FCSTD DOCUMENT  (FreeCAD 1.0R39109 (Git))
Label: bass
License: All rights reserved
LicenseURL: https://en.wikipedia.org/wiki/All_rights_reserved
objects: Sketcher::SketchObject×1, PartDesign::Body×1
note: 3 computed .brp shape members not serialized (recipe doc carries the construction recipe); baked Part::Feature solids carry a one-line shape summary decoded from their .brp

FEATURE [Sketcher::SketchObject] Sketch
  ArcFitTolerance = 1e-06
  AttachmentSupport = -> [XY_Plane]
  FullyConstrained = true
  MakeInternals = false
  MapMode = 5
  sketch-geometry (43):
    g0: LineSegment StartX=-100 StartY=100 StartZ=0 EndX=-100 EndY=21.5 EndZ=0
    g1: LineSegment StartX=-100 StartY=-100 StartZ=0 EndX=20 EndY=-100 EndZ=0
    g2: LineSegment StartX=100 StartY=-20 StartZ=0 EndX=100 EndY=100 EndZ=0
    g3: LineSegment StartX=100 StartY=100 StartZ=0 EndX=-100 EndY=100 EndZ=0
    g4: Circle CenterX=-82.5 CenterY=-82.5 CenterZ=0 NormalX=0 NormalY=0 NormalZ=1 AngleXU=0 Radius=4
    g5: LineSegment [constr] StartX=-95 StartY=-70 StartZ=0 EndX=-95 EndY=-95 EndZ=0
    g6: LineSegment [constr] StartX=-95 StartY=-95 StartZ=0 EndX=-70 EndY=-95 EndZ=0
    g7: LineSegment [constr] StartX=-70 StartY=-95 StartZ=0 EndX=-70 EndY=-70 EndZ=0
    g8: LineSegment [constr] StartX=-70 StartY=-70 StartZ=0 EndX=-95 EndY=-70 EndZ=0
    g9: Circle [constr] CenterX=-95 CenterY=-95 CenterZ=0 NormalX=0 NormalY=0 NormalZ=1 AngleXU=0 Radius=1.5
    g10: Circle [constr] CenterX=-95 CenterY=-70 CenterZ=0 NormalX=0 NormalY=0 NormalZ=1 AngleXU=0 Radius=1.5
    g11: Circle [constr] CenterX=-70 CenterY=-70 CenterZ=0 NormalX=0 NormalY=0 NormalZ=1 AngleXU=0 Radius=1.5
    g12: Circle [constr] CenterX=-70 CenterY=-95 CenterZ=0 NormalX=0 NormalY=0 NormalZ=1 AngleXU=0 Radius=1.5
    g13: LineSegment [constr] StartX=-95 StartY=95 StartZ=0 EndX=-95 EndY=70 EndZ=0
    g14: LineSegment [constr] StartX=-95 StartY=70 StartZ=0 EndX=-70 EndY=70 EndZ=0
    g15: LineSegment [constr] StartX=-70 StartY=70 StartZ=0 EndX=-70 EndY=95 EndZ=0
    g16: LineSegment [constr] StartX=-70 StartY=95 StartZ=0 EndX=-95 EndY=95 EndZ=0
    g17: Circle [constr] CenterX=-95 CenterY=95 CenterZ=0 NormalX=0 NormalY=0 NormalZ=1 AngleXU=0 Radius=1.5
    g18: Circle [constr] CenterX=-70 CenterY=95 CenterZ=0 NormalX=0 NormalY=0 NormalZ=1 AngleXU=0 Radius=1.5
    g19: Circle [constr] CenterX=-70 CenterY=70 CenterZ=0 NormalX=0 NormalY=0 NormalZ=1 AngleXU=0 Radius=1.5
    g20: Circle [constr] CenterX=-95 CenterY=70 CenterZ=0 NormalX=0 NormalY=0 NormalZ=1 AngleXU=0 Radius=1.5
    g21: Circle CenterX=-82.5 CenterY=82.5 CenterZ=0 NormalX=0 NormalY=0 NormalZ=1 AngleXU=0 Radius=4
    g22: LineSegment [constr] StartX=70 StartY=95 StartZ=0 EndX=70 EndY=70 EndZ=0
    g23: LineSegment [constr] StartX=70 StartY=70 StartZ=0 EndX=95 EndY=70 EndZ=0
    g24: LineSegment [constr] StartX=95 StartY=70 StartZ=0 EndX=95 EndY=95 EndZ=0
    g25: LineSegment [constr] StartX=95 StartY=95 StartZ=0 EndX=70 EndY=95 EndZ=0
    g26: Circle CenterX=82.5 CenterY=82.5 CenterZ=0 NormalX=0 NormalY=0 NormalZ=1 AngleXU=0 Radius=4
    g27: Circle [constr] CenterX=70 CenterY=95 CenterZ=0 NormalX=0 NormalY=0 NormalZ=1 AngleXU=0 Radius=1.5
    g28: Circle [constr] CenterX=95 CenterY=95 CenterZ=0 NormalX=0 NormalY=0 NormalZ=1 AngleXU=0 Radius=1.5
    g29: Circle [constr] CenterX=95 CenterY=70 CenterZ=0 NormalX=0 NormalY=0 NormalZ=1 AngleXU=0 Radius=1.5
    g30: Circle [constr] CenterX=70 CenterY=70 CenterZ=0 NormalX=0 NormalY=0 NormalZ=1 AngleXU=0 Radius=1.5
    g31: LineSegment StartX=-100 StartY=-21.5 StartZ=0 EndX=-64 EndY=-21.5 EndZ=0
    g32: LineSegment StartX=-64 StartY=21.5 StartZ=0 EndX=-100 EndY=21.5 EndZ=0
    g33: LineSegment StartX=-100 StartY=-21.5 StartZ=0 EndX=-100 EndY=-100 EndZ=0
    g34: Circle CenterX=-93 CenterY=-31.5 CenterZ=0 NormalX=0 NormalY=0 NormalZ=1 AngleXU=0 Radius=3.5
    g35: Circle CenterX=-71 CenterY=-31.5 CenterZ=0 NormalX=0 NormalY=0 NormalZ=1 AngleXU=0 Radius=3.5
    g36: Circle CenterX=-93 CenterY=31.5 CenterZ=0 NormalX=0 NormalY=0 NormalZ=1 AngleXU=0 Radius=3.5
    g37: Circle CenterX=-71 CenterY=31.5 CenterZ=0 NormalX=0 NormalY=0 NormalZ=1 AngleXU=0 Radius=3.5
    g38: LineSegment StartX=20 StartY=-100 StartZ=0 EndX=100 EndY=-20 EndZ=0
    g39: LineSegment [constr] StartX=-82 StartY=36.5 StartZ=0 EndX=-82 EndY=-36.5 EndZ=0
    g40: Circle [constr] CenterX=-85.5 CenterY=0 CenterZ=0 NormalX=0 NormalY=0 NormalZ=1 AngleXU=0 Radius=7.5
    g41: LineSegment StartX=-64 StartY=-21.5 StartZ=0 EndX=-64 EndY=21.5 EndZ=0
    g42: Circle CenterX=0 CenterY=0 CenterZ=0 NormalX=0 NormalY=0 NormalZ=1 AngleXU=0 Radius=57.5
  constraints (115):
    c: Coincident(g33,g1)
    c: Coincident(g2,g3)
    c: Coincident(g3,g0)
    c: Vertical(g0)
    c: Vertical(g2)
    c: Horizontal(g1)
    c: Horizontal(g3)
    c: Diameter(g4) = 8
    c: Coincident(g5,g6)
    c: Coincident(g6,g7)
    c: Coincident(g7,g8)
    c: Coincident(g8,g5)
    c: Vertical(g5)
    c: Vertical(g7)
    c: Horizontal(g6)
    c: Horizontal(g8)
    c: Equal(g7,g6)
    c: Symmetric(g5,g6,g4)
    c: Coincident(g9,g5)
    c: Coincident(g10,g5)
    c: Coincident(g11,g7)
    c: Coincident(g12,g6)
    c: Equal(g9,g10)
    c: Equal(g10,g11)
    c: Equal(g11,g12)
    c: Diameter(g12) = 3
    c: DistanceY(g33,g5) = 5
    c: Distance(g5,g0) = 5
    c: DistanceX(g8,g8) = 25
    c: Coincident(g13,g14)
    c: Coincident(g14,g15)
    c: Coincident(g15,g16)
    c: Coincident(g16,g13)
    c: Vertical(g13)
    c: Vertical(g15)
    c: Horizontal(g14)
    c: Horizontal(g16)
    c: Coincident(g17,g13)
    c: Coincident(g18,g15)
    c: Coincident(g19,g14)
    c: Coincident(g20,g13)
    c: Equal(g17,g18)
    c: Equal(g18,g19)
    c: Equal(g19,g20)
    c: Symmetric(g13,g14,g21)
    c: Equal(g15,g14)
    c: DistanceY(g13,g0) = 5
    c: DistanceX(g0,g13) = 5
    c: DistanceX(g16,g16) = 25
    c: Equal(g20,g10)
    c: Equal(g4,g21)
    c: Coincident(g22,g23)
    c: Coincident(g23,g24)
    c: Coincident(g24,g25)
    c: Coincident(g25,g22)
    c: Vertical(g22)
    c: Vertical(g24)
    c: Horizontal(g23)
    c: Horizontal(g25)
    c: Coincident(g27,g22)
    c: Coincident(g28,g24)
    c: Coincident(g29,g23)
    c: Coincident(g30,g22)
    c: Equal(g30,g27)
    c: Equal(g27,g28)
    c: Equal(g28,g29)
    c: Symmetric(g22,g23,g26)
    c: Equal(g22,g25)
    c: Equal(g25,g16)
    c: Equal(g21,g26)
    c: Equal(g27,g18)
    c: DistanceY(g24,g2) = 5
    c: DistanceX(g24,g2) = 5
    c: DistanceX(g0,g-1) = 100
    c: Horizontal(g31)
    c: Horizontal(g32)
    c: PointOnObject(g31,g33)
    c: Coincident(g0,g32)
    c: PointOnObject(g33,g31)
    c: Vertical(g33)
    c: Vertical(g31,g0)
    c: Horizontal(g36,g37)
    c: Horizontal(g34,g35)
    c: Equal(g36,g37)
    c: Equal(g37,g35)
    c: Equal(g35,g34)
    c: Vertical(g34,g36)
    c: DistanceX(g36,g37) = 22
    c: Diameter(g37) = 7
    c: Coincident(g2,g38)
    c: Coincident(g1,g38)
    c: DistanceY(g-1,g2) = 100
    c: DistanceY(g1,g-1) = 100
    c: DistanceY(g2,g-1) = 20
    c: DistanceX(g-1,g1) = 20
    c: DistanceX(g3,g3) = 200
    c: Vertical(g39)
    c: DistanceY(g39,g39) = 73
    c: DistanceY(g-1,g39) = 36.5
    c: Vertical(g37,g35)
    c: DistanceX(g0,g36) = 7
    c: DistanceX(g39,g35) = 11
    c: PointOnObject(g40,g-1)
    c: Diameter(g40) = 15
    c: DistanceX(g0,g40) = 14.5
    c: Vertical(g41)
    c: DistanceX(g40,g41) = 21.5
    c: Coincident(g32,g41)
    c: Coincident(g31,g41)
    c: Coincident(g42,g-1)
    c: DistanceY(g-1,g32) = 21.5
    c: DistanceY(g41,g41) = 43
    c: DistanceY(g0,g36) = 10
    c: DistanceY(g34,g31) = 10
    c: Diameter(g42) = 115
FEATURE [PartDesign::Body] Body
  AllowCompound = false
  Group = -> [Sketch]
  Origin = -> Origin
